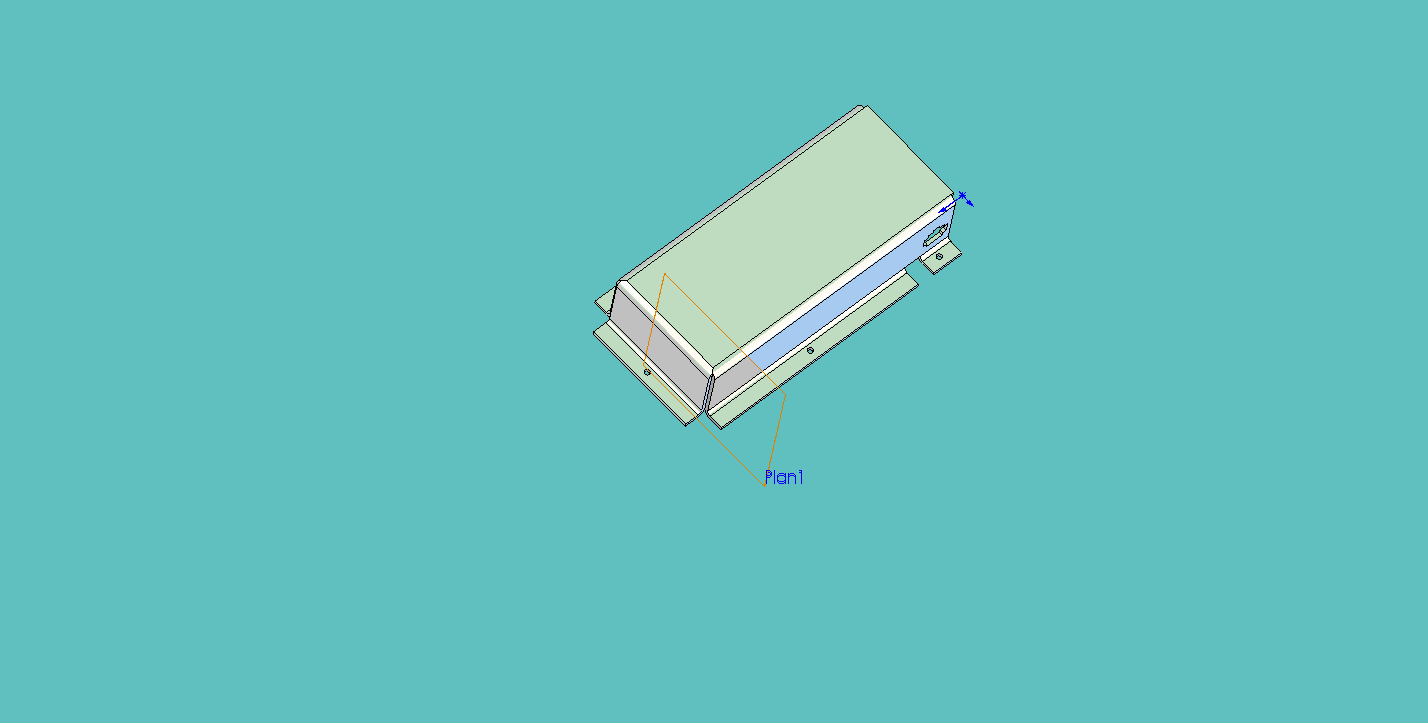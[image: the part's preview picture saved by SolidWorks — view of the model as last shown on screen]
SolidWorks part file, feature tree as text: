
SOLIDWORKS PART (.sldprt)
format: sldprt  version: not decoded by parser v0  size: 546,816 bytes
history: native  units: mm
features: sketch x6, plane x4, cut_extrude x4, extrude x2, fillet x2, material x1, shell x1 (+10 scaffold rows collapsed)
feature tree (30):
  scaffold x10  (default folders/planes/origin — collapsed)
  material  "Matériau <non spécifié>"
  plane  "Plan de face"
  plane  "Plan de dessus"
  plane  "Plan de droite"
  sketch  "Esquisse1"  dims[c1.D1=2.0mm c1.D2=10.0mm c1.D3=2.0mm c1.D4=2.0mm c1.D5=37.0mm c1.D6=69.0mm c2.D1=161.0mm c2.D2=69.0mm]
  extrude  "Extrusion2"  Depth=35mm
  sketch  "Esquisse2"  dims[D1=10.0mm]
  extrude  "Extrusion3"  Depth=35mm
  shell  "Coque1"  Thickness=2mm
  sketch  "Esquisse3"  dims[c1.D1=0.01mm c1.D2=0.01mm c1.D3=~3.164858mm c2.D3=45.0deg c2.D4=2.0mm c2.D5=~4.25067mm c3.D5=45.0deg c3.D6=2.0mm]
  cut_extrude  "Enlèv. mat.-Extru.1"  [1 undecoded]
  sketch  "Esquisse4"  dims[D1=2.0mm D2=18.0mm D3=10.0mm D4=4.0mm D5=10.0mm D6=10.0mm D7=4.0mm D8=2.5mm D9=5.6mm D10=1.6mm D11=15.0mm D12=10.0mm]
  cut_extrude  "Enlèv. mat.-Extru.2"  Depth=14mm
  fillet  "Congé3"  Radius=2mm
  fillet  "Congé4"  Radius=4mm
  plane  "Plan1"
  sketch  "Esquisse6"  dims[D8=3.2mm D1=5.0mm D2=5.0mm D3=5.0mm D4=93.0mm D5=93.0mm D6=20.0mm D7=10.0mm D9=11.0mm D10=14.0mm]
  cut_extrude  "Enlèv. mat.-Extru.3"  Depth=4mm
  sketch  "Esquisse7"  dims[D1=4.0mm D2=2.0mm]
  cut_extrude  "Enlèv. mat.-Extru.4"  [1 undecoded]
decode coverage: 13 of 15 modeling features carry decoded parameters
note: ~ marks probable driven/reference dimensions
note: 2 parameter values undecoded
note: suppression state not decoded; provenance and decode notes live in map.json
